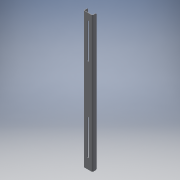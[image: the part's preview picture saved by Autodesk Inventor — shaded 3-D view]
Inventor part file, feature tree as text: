
AUTODESK INVENTOR PART (.ipt)
format: ipt  version: 2016 (Build 200138000, 138)  size: 161,792 bytes
history: native  units: mm
features: sheet_metal_op x2, sketch x2, chamfer x1, extrude x1, pattern_linear x1, other x1
ambient origin geometry x8: Origin, YZ Plane, XZ Plane, XY Plane, X Axis, Y Axis, Z Axis, Center Point
bodies: Solid1 (feature_tree)
feature tree (8):
  sheet_metal_op  "Contour Flange1"
  chamfer  "Corner Round1"
  extrude  "Extrusion1"  Depth=20.0mm
  pattern_linear  "Rectangular Pattern1"  Spacing1=3.0mm  [1 undecoded]
  sketch  "Sketch1"  dims[d0=20.0mm d1=20.0mm]
  other  "Plate1"
  sheet_metal_op  "Bend1"
  sketch  "Sketch2"  dims[d2=44.0mm d3=3.0mm d4=1.5mm d5=6.0mm d6=3.0mm d8=3.0mm d9=3.0mm d10=12.0mm d11=3.0mm d12=3.0mm d13=6.0mm d16=9.525mm d18=9.525mm d19=9.525mm d21=10.0mm d22=0.0mm d23=20.0mm d25=461.25mm]
note: 1 required parameter value undecoded (feature->parameter linkage not recoverable at this tier; creation-order binding heuristic only, values carry confidence <= 0.55)
